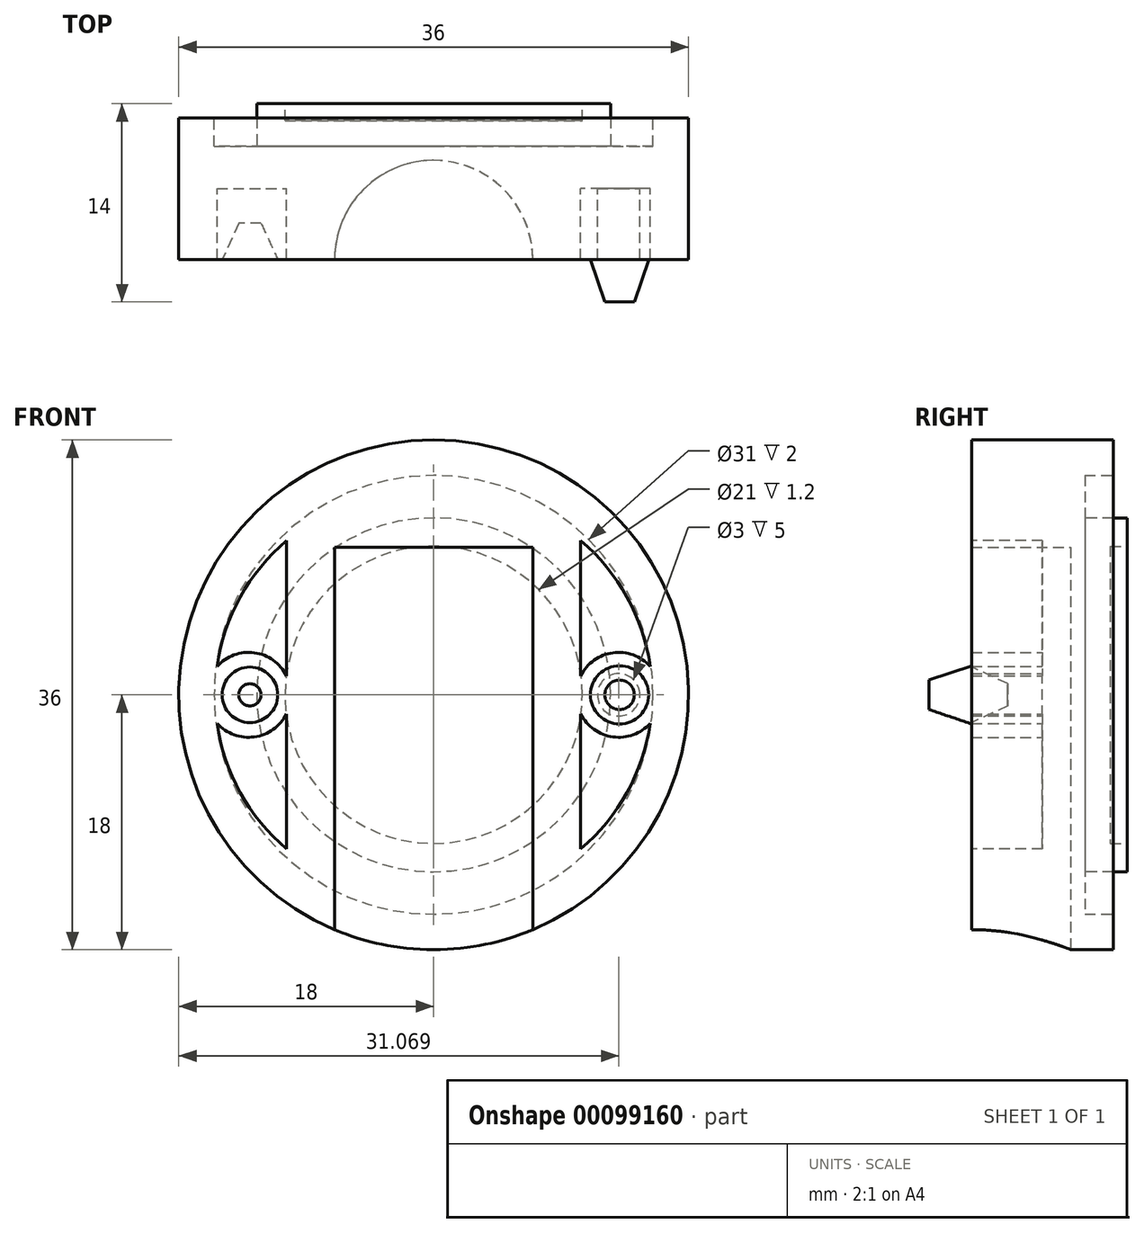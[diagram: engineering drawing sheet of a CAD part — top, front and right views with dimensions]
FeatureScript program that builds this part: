
annotation { "Feature Type Name" : "Feature", "Feature Type Description" : "" }
export const myFeature = defineFeature(function(context is Context, id is Id, definition is map)
    precondition{}
    {
        {
            var Q0;
            Q0=qCreatedBy(makeId("Front.planeOp"),FACE);
            var sketch = newSketch(context, id + "F0", { "sketchPlane" : qUnion([Q0])});
            skCircle(sketch, "E0", {"center": v(0, 0) * mm, "radius": 18 * mm});
            skSolve(sketch);
        }
        {
            var Q0;
            Q0=makeQuery(id+"F0.imprint","IMPRINT",FACE,{"disambiguationData":[TD([[makeQuery(id+"F0.imprint","IMPRINT",EDGE,{"derivedFrom":sQuery(id+"F0.wireOp",EDGE,"E0")}),1.0]])]});
            extrude(context, id + "F1", {"entities" : qUnion([Q0]), "oppositeDirection" : true, "depth" : 10 * mm});
        }
        {
            var Q0;
            Q0=makeQuery(id+"F1.opExtrude","CAP_FACE",FACE,{"disambiguationData":[OSD([sQuery(id+"F0.wireOp",EDGE,"E0")])],"isStart":false});
            var sketch = newSketch(context, id + "F2", { "sketchPlane" : qUnion([Q0])});
            skCircle(sketch, "E1", {"center": v(0, 0) * mm, "radius": 15.5 * mm});
            skSolve(sketch);
        }
        {
            var Q0;
            Q0=makeQuery(id+"F2.imprint","IMPRINT",FACE,{"disambiguationData":[TD([[makeQuery(id+"F2.imprint","IMPRINT",EDGE,{"derivedFrom":sQuery(id+"F2.wireOp",EDGE,"E1")}),1.0]])]});
            extrude(context, id + "F3", {"entities" : qUnion([Q0]), "operationType" : NewBodyOperationType.REMOVE, "oppositeDirection" : true, "depth" : 2 * mm});
        }
        {
            var Q0;
            Q0=makeQuery(id+"F1.opExtrude","CAP_FACE",FACE,{"disambiguationData":[OSD([sQuery(id+"F0.wireOp",EDGE,"E0")])],"isStart":true});
            var sketch = newSketch(context, id + "F4", { "sketchPlane" : qUnion([Q0])});
            skArc(sketch, "E2", {"start": v(10.4, 10.89) * mm, "mid": v(15.43, 0) * mm, "end": v(10.4, -10.89) * mm});
            skLineSegment(sketch, "E3", {"start": v(10.4, 10.89) * mm, "end": v(10.4, -10.89) * mm});
            skLineSegment(sketch, "E4.MirrorCS", {"start": v(-10.4, 10.89) * mm, "end": v(-10.4, -10.89) * mm});
            skArc(sketch, "E5.MirrorCS", {"start": v(-10.4, 10.89) * mm, "mid": v(-15.43, 0) * mm, "end": v(-10.4, -10.89) * mm});
            skSolve(sketch);
        }
        {
            var Q0;
            Q0 = qSketchRegion(id + "F4", true);
            extrude(context, id + "F5", {"entities" : qUnion([Q0]), "operationType" : NewBodyOperationType.REMOVE, "oppositeDirection" : true, "depth" : 5 * mm});
        }
        {
            var Q0;
            Q0=makeQuery(id+"F5.boolean.opBoolean","COPY",FACE,{"derivedFrom":makeQuery(id+"F5.opExtrude","CAP_FACE",FACE,{"disambiguationData":[OSD([sQuery(id+"F4.wireOp",EDGE,"E4.MirrorCS"),sQuery(id+"F4.wireOp",EDGE,"E5.MirrorCS")])],"isStart":false})});
            var sketch = newSketch(context, id + "F6", { "sketchPlane" : qUnion([Q0])});
            skCircle(sketch, "E6", {"center": v(-13.07, 0) * mm, "radius": 3 * mm});
            skCircle(sketch, "E7.MirrorC", {"center": v(13.07, 0) * mm, "radius": 3 * mm});
            skCircle(sketch, "E8.MirrorC", {"center": v(13.07, 0) * mm, "radius": 1.5 * mm});
            skSolve(sketch);
        }
        {
            var Q0;
            Q0 = qSketchRegion(id + "F6", true);
            extrude(context, id + "F7", {"entities" : qUnion([Q0]), "operationType" : NewBodyOperationType.ADD, "depth" : 5 * mm});
        }
        {
            var Q0;
            Q0=makeQuery(id+"F3.boolean.opBoolean","COPY",FACE,{"derivedFrom":makeQuery(id+"F3.opExtrude","CAP_FACE",FACE,{"disambiguationData":[OSD([sQuery(id+"F2.wireOp",EDGE,"E1")])],"isStart":false})});
            var sketch = newSketch(context, id + "F8", { "sketchPlane" : qUnion([Q0])});
            skCircle(sketch, "E9", {"center": v(0, 0) * mm, "radius": 12.5 * mm});
            skSolve(sketch);
        }
        {
            var Q0;
            Q0 = qSketchRegion(id + "F8", true);
            extrude(context, id + "F9", {"entities" : qUnion([Q0]), "operationType" : NewBodyOperationType.ADD, "depth" : 3 * mm});
        }
        {
            var Q0;
            Q0=makeQuery(id+"F9.opExtrude","CAP_FACE",FACE,{"disambiguationData":[OSD([sQuery(id+"F8.wireOp",EDGE,"E9")])],"isStart":false});
            var sketch = newSketch(context, id + "F10", { "sketchPlane" : qUnion([Q0])});
            skCircle(sketch, "E10", {"center": v(0, 0) * mm, "radius": 10.5 * mm});
            skSolve(sketch);
        }
        {
            var Q0;
            Q0=makeQuery(id+"F10.imprint","IMPRINT",FACE,{"disambiguationData":[TD([[makeQuery(id+"F10.imprint","IMPRINT",EDGE,{"derivedFrom":sQuery(id+"F10.wireOp",EDGE,"E10")}),1.0]])]});
            extrude(context, id + "F11", {"entities" : qUnion([Q0]), "operationType" : NewBodyOperationType.REMOVE, "oppositeDirection" : true, "depth" : 1.2 * mm});
        }
        {
            var Q0;
            Q0=qCreatedBy(makeId("Top.planeOp"),FACE);
            var sketch = newSketch(context, id + "F12", { "sketchPlane" : qUnion([Q0])});
            skLineSegment(sketch, "E11", {"start": v(11.08, 0) * mm, "end": v(12.09, -3) * mm});
            skLineSegment(sketch, "E12", {"start": v(12.09, -3) * mm, "end": v(13.13, -3) * mm});
            skLineSegment(sketch, "E13", {"start": v(13.13, -10.58) * mm, "end": v(13.13, 15.13) * mm, "construction": true});
            skLineSegment(sketch, "E14", {"start": v(11.08, 0) * mm, "end": v(13.13, 0) * mm});
            skLineSegment(sketch, "E15", {"start": v(13.13, 0) * mm, "end": v(13.13, -3) * mm});
            skSolve(sketch);
        }
        {
            var Q0;
            Q0 = qSketchRegion(id + "F12", true);
            var Q1;
            Q1=sQuery(id+"F12.wireOp",EDGE,"E13");
            revolve(context, id + "F13", {"operationType" : NewBodyOperationType.ADD, "entities" : qUnion([Q0]), "axis" : qUnion([Q1]), "revolveType" : RevolveType.FULL});
        }
        {
            var Q0;
            Q0=qCreatedBy(makeId("Top.planeOp"),FACE);
            var sketch = newSketch(context, id + "F14", { "sketchPlane" : qUnion([Q0])});
            skLineSegment(sketch, "E16", {"start": v(-14.93, 0) * mm, "end": v(-13.76, 2.55) * mm});
            skLineSegment(sketch, "E17", {"start": v(-13.76, 2.55) * mm, "end": v(-12.97, 2.55) * mm});
            skLineSegment(sketch, "E18", {"start": v(-12.97, 7.02) * mm, "end": v(-12.97, -10.78) * mm, "construction": true});
            skLineSegment(sketch, "E19", {"start": v(-14.93, 0) * mm, "end": v(-12.97, 0) * mm});
            skLineSegment(sketch, "E20", {"start": v(-12.97, 2.55) * mm, "end": v(-12.97, 0) * mm});
            skSolve(sketch);
        }
        {
            var Q0;
            Q0 = qSketchRegion(id + "F14", true);
            var Q1;
            Q1=sQuery(id+"F14.wireOp",EDGE,"E18");
            revolve(context, id + "F15", {"operationType" : NewBodyOperationType.REMOVE, "entities" : qUnion([Q0]), "axis" : qUnion([Q1]), "revolveType" : RevolveType.FULL, "oppositeDirection" : true});
        }
        {
            var Q0;
            {var subQ0=sQuery(id+"F6.wireOp",EDGE,"E6");Q0=makeQuery(id+"FBLCLFlpZ4dugoh_1.boolean.opBoolean","MERGE",FACE,{"derivedFrom":[makeQuery(id+"FWsEwnThb9P5rB2_1.boolean.opBoolean","MERGE",FACE,{"derivedFrom":[makeQuery(id+"F7.boolean.opBoolean","MERGE",FACE,{"derivedFrom":[makeQuery(id+"F1.opExtrude","CAP_FACE",FACE,{"disambiguationData":[OSD([sQuery(id+"F0.wireOp",EDGE,"E0")])],"isStart":true}),makeQuery(id+"F7.opExtrude","CAP_FACE",FACE,{"disambiguationData":[OSD([sQuery(id+"F4.wireOp",EDGE,"E4.MirrorCS"),sQuery(id+"F4.wireOp",EDGE,"E5.MirrorCS"),sQuery(id+"F6.wireOp",EDGE,"hpcp9vng-u04X-4P3l-DaGh-LNbDTDDy2Gux"),subQ0])],"isStart":false}),makeQuery(id+"F7.opExtrude","CAP_FACE",FACE,{"disambiguationData":[OSD([sQuery(id+"F6.wireOp",EDGE,"E7.MirrorC"),sQuery(id+"F6.wireOp",EDGE,"E8.MirrorC")])],"isStart":false})]}),makeQuery(id+"FWsEwnThb9P5rB2_1.opExtrude","CAP_FACE",FACE,{"disambiguationData":[OSD([subQ0])],"isStart":false})]}),makeQuery(id+"FBLCLFlpZ4dugoh_1.opExtrude","CAP_FACE",FACE,{"disambiguationData":[OSD([sQuery(id+"F4.wireOp",EDGE,"E2"),sQuery(id+"F4.wireOp",EDGE,"E3")])],"isStart":false})]});}
            var sketch = newSketch(context, id + "F16", { "sketchPlane" : qUnion([Q0])});
            skLineSegment(sketch, "E21.bottom", {"start": v(0, 10.41) * mm, "end": v(7, 10.41) * mm});
            skLineSegment(sketch, "E22", {"start": v(0, 17.8) * mm, "end": v(0, -24.54) * mm, "construction": true});
            skLineSegment(sketch, "E23", {"start": v(0, 10.41) * mm, "end": v(0, -19.6) * mm});
            skLineSegment(sketch, "E24", {"start": v(0, -19.6) * mm, "end": v(7, -19.6) * mm});
            skLineSegment(sketch, "E25", {"start": v(7, 10.41) * mm, "end": v(7, -19.6) * mm});
            skSolve(sketch);
        }
        {
            var Q0;
            {var subQ0=sQuery(id+"F16.wireOp",EDGE,"E21.bottom");Q0=makeQuery(id+"F16.imprint","IMPRINT",FACE,{"disambiguationData":[TD([[makeQuery(id+"F16.imprint","IMPRINT",EDGE,{"derivedFrom":subQ0}),-1.0]])]});}
            var Q1;
            {var subQ0=sQuery(id+"F16.wireOp",EDGE,"E24");Q1=makeQuery(id+"F16.imprint","IMPRINT",FACE,{"disambiguationData":[TD([[makeQuery(id+"F16.imprint","IMPRINT",EDGE,{"derivedFrom":subQ0}),1.0]])]});}
            var Q2;
            Q2=sQuery(id+"F16.wireOp",EDGE,"E22");
            revolve(context, id + "F17", {"operationType" : NewBodyOperationType.REMOVE, "entities" : qUnion([Q0, Q1]), "axis" : qUnion([Q2]), "revolveType" : RevolveType.ONE_DIRECTION, "oppositeDirection" : true, "angle" : 180 * degree});
        }
    });
